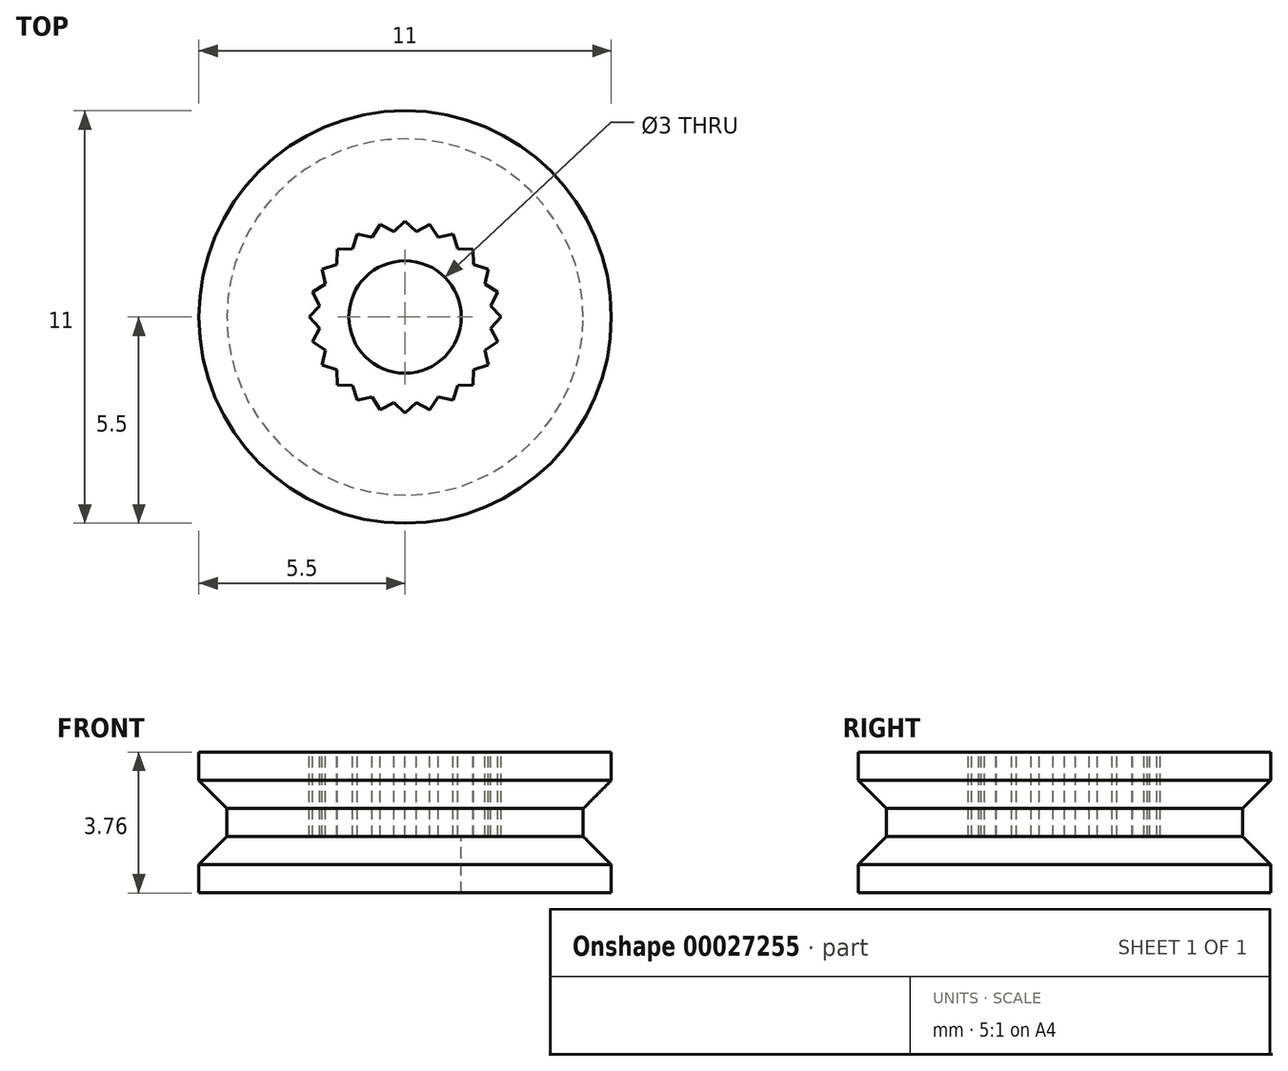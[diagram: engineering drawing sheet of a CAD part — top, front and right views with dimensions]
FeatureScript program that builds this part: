
annotation { "Feature Type Name" : "Feature", "Feature Type Description" : "" }
export const myFeature = defineFeature(function(context is Context, id is Id, definition is map)
    precondition{}
    {
        {
            var Q0;
            Q0=qCreatedBy(makeId("Front.planeOp"),FACE);
            var sketch = newSketch(context, id + "F0", { "sketchPlane" : qUnion([Q0])});
            skLineSegment(sketch, "E0", {"start": v(-1.88, 0) * mm, "end": v(-1.88, 6.25) * mm});
            skLineSegment(sketch, "E1", {"start": v(-1.88, 6.25) * mm, "end": v(-0.38, 4.75) * mm});
            skLineSegment(sketch, "E2", {"start": v(-0.38, 4.75) * mm, "end": v(0.37, 4.75) * mm});
            skLineSegment(sketch, "E3", {"start": v(0.37, 4.75) * mm, "end": v(1.88, 6.25) * mm});
            skLineSegment(sketch, "E4", {"start": v(1.87, 6.25) * mm, "end": v(1.87, 0) * mm});
            skLineSegment(sketch, "E5", {"start": v(1.87, 0) * mm, "end": v(-1.87, 0) * mm});
            skPoint(sketch, "E6", {"position": v(0, 0) * mm});
            skLineSegment(sketch, "E7", {"start": v(-1.88, 5.5) * mm, "end": v(1.87, 5.5) * mm});
            skSolve(sketch);
        }
        {
            var Q0;
            {var subQ10=sQuery(id+"F0.wireOp",EDGE,"E2");Q0=makeQuery(id+"F0.imprint","IMPRINT",FACE,{"disambiguationData":[TD([[makeQuery(id+"F0.imprint","IMPRINT",EDGE,{"derivedFrom":subQ10}),-1.0]])]});}
            var Q1;
            Q1=sQuery(id+"F0.wireOp",EDGE,"E5");
            revolve(context, id + "F1", {"entities" : qUnion([Q0]), "axis" : qUnion([Q1]), "revolveType" : RevolveType.FULL});
        }
        {
            var Q0;
            Q0=makeQuery(id+"F1.opRevolve","SWEPT_FACE",FACE,{"disambiguationData":[OSD([sQuery(id+"F0.wireOp",EDGE,"E4")])]});
            var sketch = newSketch(context, id + "F2", { "sketchPlane" : qUnion([Q0])});
            skCircle(sketch, "E8", {"center": v(0, 0) * mm, "radius": 2.3 * mm, "construction": true});
            skFitSpline(sketch, "E9.4", {"points": [v(-0.66, 2.47) * mm, v(-0.54, 2.4) * mm, v(-0.42, 2.34) * mm, v(-0.3, 2.28) * mm]});
            skFitSpline(sketch, "E9.18", {"points": [v(2.28, -0.3) * mm, v(2.34, -0.42) * mm, v(2.4, -0.54) * mm, v(2.47, -0.66) * mm]});
            skFitSpline(sketch, "E9.32", {"points": [v(-0.66, -2.47) * mm, v(-0.73, -2.35) * mm, v(-0.8, -2.24) * mm, v(-0.88, -2.12) * mm]});
            skFitSpline(sketch, "E9.33", {"points": [v(-0.88, -2.12) * mm, v(-1.01, -2.15) * mm, v(-1.15, -2.18) * mm, v(-1.28, -2.21) * mm]});
            skFitSpline(sketch, "E9.7", {"points": [v(0.3, 2.28) * mm, v(0.42, 2.34) * mm, v(0.54, 2.4) * mm, v(0.66, 2.47) * mm]});
            skCircle(sketch, "E10", {"center": v(0, 0) * mm, "radius": 2.56 * mm, "construction": true});
            skFitSpline(sketch, "E9.34", {"points": [v(-1.28, -2.21) * mm, v(-1.32, -2.08) * mm, v(-1.36, -1.95) * mm, v(-1.4, -1.82) * mm]});
            skFitSpline(sketch, "E9.16", {"points": [v(2.47, 0.66) * mm, v(2.4, 0.54) * mm, v(2.34, 0.42) * mm, v(2.28, 0.3) * mm]});
            skFitSpline(sketch, "E9.13", {"points": [v(1.82, 1.4) * mm, v(1.95, 1.36) * mm, v(2.08, 1.32) * mm, v(2.21, 1.28) * mm]});
            skFitSpline(sketch, "E9.25", {"points": [v(1.4, -1.82) * mm, v(1.36, -1.95) * mm, v(1.32, -2.08) * mm, v(1.28, -2.21) * mm]});
            skFitSpline(sketch, "E9.38", {"points": [v(-2.21, -1.28) * mm, v(-2.18, -1.15) * mm, v(-2.15, -1.01) * mm, v(-2.12, -0.88) * mm]});
            skFitSpline(sketch, "E9.14", {"points": [v(2.21, 1.28) * mm, v(2.18, 1.15) * mm, v(2.15, 1.01) * mm, v(2.12, 0.88) * mm]});
            skFitSpline(sketch, "E9.12", {"points": [v(1.8, 1.8) * mm, v(1.81, 1.67) * mm, v(1.82, 1.54) * mm, v(1.82, 1.4) * mm]});
            skFitSpline(sketch, "E9.31", {"points": [v(-0.3, -2.28) * mm, v(-0.42, -2.34) * mm, v(-0.54, -2.4) * mm, v(-0.66, -2.47) * mm]});
            skFitSpline(sketch, "E9.8", {"points": [v(0.66, 2.47) * mm, v(0.73, 2.35) * mm, v(0.8, 2.24) * mm, v(0.88, 2.12) * mm]});
            skFitSpline(sketch, "E9.39", {"points": [v(-2.12, -0.88) * mm, v(-2.24, -0.8) * mm, v(-2.35, -0.73) * mm, v(-2.47, -0.66) * mm]});
            skFitSpline(sketch, "E9.23", {"points": [v(1.82, -1.4) * mm, v(1.82, -1.54) * mm, v(1.81, -1.67) * mm, v(1.8, -1.8) * mm]});
            skFitSpline(sketch, "E9.47", {"points": [v(-2.12, 0.88) * mm, v(-2.15, 1.01) * mm, v(-2.18, 1.15) * mm, v(-2.21, 1.28) * mm]});
            skFitSpline(sketch, "E9.9", {"points": [v(0.88, 2.12) * mm, v(1.01, 2.15) * mm, v(1.15, 2.18) * mm, v(1.28, 2.21) * mm]});
            skFitSpline(sketch, "E9.36", {"points": [v(-1.8, -1.8) * mm, v(-1.81, -1.67) * mm, v(-1.82, -1.54) * mm, v(-1.82, -1.4) * mm]});
            skFitSpline(sketch, "E9.20", {"points": [v(2.47, -0.66) * mm, v(2.35, -0.73) * mm, v(2.24, -0.8) * mm, v(2.12, -0.88) * mm]});
            skFitSpline(sketch, "E9.15", {"points": [v(2.12, 0.88) * mm, v(2.24, 0.8) * mm, v(2.35, 0.73) * mm, v(2.47, 0.66) * mm]});
            skFitSpline(sketch, "E9.2", {"points": [v(-1.28, 2.21) * mm, v(-1.15, 2.18) * mm, v(-1.01, 2.15) * mm, v(-0.88, 2.12) * mm]});
            skFitSpline(sketch, "E9.26", {"points": [v(1.28, -2.21) * mm, v(1.15, -2.18) * mm, v(1.01, -2.15) * mm, v(0.88, -2.12) * mm]});
            skFitSpline(sketch, "E9.30", {"points": [v(0, -2.56) * mm, v(-0.1, -2.46) * mm, v(-0.2, -2.37) * mm, v(-0.3, -2.28) * mm]});
            skFitSpline(sketch, "E9.43", {"points": [v(-2.28, 0.3) * mm, v(-2.34, 0.42) * mm, v(-2.4, 0.54) * mm, v(-2.47, 0.66) * mm]});
            skFitSpline(sketch, "E9.10", {"points": [v(1.28, 2.21) * mm, v(1.32, 2.08) * mm, v(1.36, 1.95) * mm, v(1.4, 1.82) * mm]});
            skFitSpline(sketch, "E9.11", {"points": [v(1.4, 1.82) * mm, v(1.54, 1.82) * mm, v(1.67, 1.81) * mm, v(1.8, 1.8) * mm]});
            skFitSpline(sketch, "E9.35", {"points": [v(-1.4, -1.82) * mm, v(-1.54, -1.82) * mm, v(-1.67, -1.81) * mm, v(-1.8, -1.8) * mm]});
            skFitSpline(sketch, "E9.21", {"points": [v(2.12, -0.88) * mm, v(2.15, -1.01) * mm, v(2.18, -1.15) * mm, v(2.21, -1.28) * mm]});
            skFitSpline(sketch, "E9.37", {"points": [v(-1.82, -1.4) * mm, v(-1.95, -1.36) * mm, v(-2.08, -1.32) * mm, v(-2.21, -1.28) * mm]});
            skFitSpline(sketch, "E9.40", {"points": [v(-2.47, -0.66) * mm, v(-2.4, -0.54) * mm, v(-2.34, -0.42) * mm, v(-2.28, -0.3) * mm]});
            skFitSpline(sketch, "E9.24", {"points": [v(1.8, -1.8) * mm, v(1.67, -1.81) * mm, v(1.54, -1.82) * mm, v(1.4, -1.82) * mm]});
            skFitSpline(sketch, "E9.29", {"points": [v(0.3, -2.28) * mm, v(0.2, -2.37) * mm, v(0.1, -2.46) * mm, v(0, -2.56) * mm]});
            skFitSpline(sketch, "E9.45", {"points": [v(-1.82, 1.4) * mm, v(-1.82, 1.54) * mm, v(-1.81, 1.67) * mm, v(-1.8, 1.8) * mm]});
            skFitSpline(sketch, "E9.41", {"points": [v(-2.28, -0.3) * mm, v(-2.37, -0.2) * mm, v(-2.46, -0.1) * mm, v(-2.56, 0) * mm]});
            skFitSpline(sketch, "E9.44", {"points": [v(-2.47, 0.66) * mm, v(-2.35, 0.73) * mm, v(-2.24, 0.8) * mm, v(-2.12, 0.88) * mm]});
            skFitSpline(sketch, "E9.28", {"points": [v(0.66, -2.47) * mm, v(0.54, -2.4) * mm, v(0.42, -2.34) * mm, v(0.3, -2.28) * mm]});
            skFitSpline(sketch, "E9.0", {"points": [v(-1.8, 1.8) * mm, v(-1.67, 1.81) * mm, v(-1.54, 1.82) * mm, v(-1.4, 1.82) * mm]});
            skFitSpline(sketch, "E9.5", {"points": [v(-0.3, 2.28) * mm, v(-0.2, 2.37) * mm, v(-0.1, 2.46) * mm, v(0, 2.56) * mm]});
            skFitSpline(sketch, "E9.27", {"points": [v(0.88, -2.12) * mm, v(0.8, -2.24) * mm, v(0.73, -2.35) * mm, v(0.66, -2.47) * mm]});
            skFitSpline(sketch, "E9.1", {"points": [v(-1.4, 1.82) * mm, v(-1.36, 1.95) * mm, v(-1.32, 2.08) * mm, v(-1.28, 2.21) * mm]});
            skFitSpline(sketch, "E9.6", {"points": [v(0, 2.56) * mm, v(0.1, 2.46) * mm, v(0.2, 2.37) * mm, v(0.3, 2.28) * mm]});
            skFitSpline(sketch, "E9.22", {"points": [v(2.21, -1.28) * mm, v(2.08, -1.32) * mm, v(1.95, -1.36) * mm, v(1.82, -1.4) * mm]});
            skFitSpline(sketch, "E9.42", {"points": [v(-2.56, 0) * mm, v(-2.46, 0.1) * mm, v(-2.37, 0.2) * mm, v(-2.28, 0.3) * mm]});
            skFitSpline(sketch, "E9.3", {"points": [v(-0.88, 2.12) * mm, v(-0.8, 2.24) * mm, v(-0.73, 2.35) * mm, v(-0.66, 2.47) * mm]});
            skFitSpline(sketch, "E9.17", {"points": [v(2.28, 0.3) * mm, v(2.37, 0.2) * mm, v(2.46, 0.1) * mm, v(2.56, 0) * mm]});
            skFitSpline(sketch, "E9.46", {"points": [v(-2.21, 1.28) * mm, v(-2.08, 1.32) * mm, v(-1.95, 1.36) * mm, v(-1.82, 1.4) * mm]});
            skFitSpline(sketch, "E9.19", {"points": [v(2.56, 0) * mm, v(2.46, -0.1) * mm, v(2.37, -0.2) * mm, v(2.28, -0.3) * mm]});
            skLineSegment(sketch, "E11", {"start": v(-1.82, 1.4) * mm, "end": v(1.82, -1.4) * mm, "construction": true});
            skCircle(sketch, "E12", {"center": v(0, 0) * mm, "radius": 1.5 * mm});
            skSolve(sketch);
        }
        {
            var Q0;
            Q0=makeQuery(id+"F2.imprint","IMPRINT",FACE,{"disambiguationData":[TD([[makeQuery(id+"F2.imprint","IMPRINT",EDGE,{"derivedFrom":sQuery(id+"F2.wireOp",EDGE,"E9.32")}),-1.0]])]});
            var Q1;
            Q1=makeQuery(id+"F2.imprint","IMPRINT",FACE,{"disambiguationData":[TD([[makeQuery(id+"F2.imprint","IMPRINT",EDGE,{"derivedFrom":sQuery(id+"F2.wireOp",EDGE,"E9.4")}),-1.0]])]});
            extrude(context, id + "F3", {"entities" : qUnion([Q0, Q1]), "operationType" : NewBodyOperationType.REMOVE, "oppositeDirection" : true, "depth" : 2.25 * mm});
        }
        {
            var Q0;
            Q0=makeQuery(id+"F2.imprint","IMPRINT",FACE,{"disambiguationData":[TD([[makeQuery(id+"F2.imprint","IMPRINT",EDGE,{"derivedFrom":sQuery(id+"F2.wireOp",EDGE,"E12")}),1.0]])]});
            var Q1;
            Q1=sQuery(id+"F2.wireOp",EDGE,"E12");
            extrude(context, id + "F4", {"entities" : qUnion([Q0]), "operationType" : NewBodyOperationType.REMOVE, "surfaceEntities" : qUnion([Q1]), "endBound" : BoundingType.THROUGH_ALL, "oppositeDirection" : true, "depth" : 25 * mm});
        }
        {
            var Q0;
            Q0=qCreatedBy(makeId("Top.planeOp"),FACE);
            var sketch = newSketch(context, id + "F5", { "sketchPlane" : qUnion([Q0])});
            skLineSegment(sketch, "E13", {"start": v(-14, 0) * mm, "end": v(17.64, 0) * mm});
            skLineSegment(sketch, "E14", {"start": v(0, -21.28) * mm, "end": v(0, 27.28) * mm});
            skSolve(sketch);
        }
        {
            var Q0;
            Q0=makeQuery(id+"F1.opRevolve","SWEPT_BODY",BODY,{"disambiguationData":[OSD([sQuery(id+"F0.wireOp",EDGE,"E0"),sQuery(id+"F0.wireOp",EDGE,"E1"),sQuery(id+"F0.wireOp",EDGE,"E2"),sQuery(id+"F0.wireOp",EDGE,"E3"),sQuery(id+"F0.wireOp",EDGE,"E4"),sQuery(id+"F0.wireOp",EDGE,"E5"),sQuery(id+"F0.wireOp",EDGE,"E7")])]});
            var Q1;
            Q1=sQuery(id+"F5.wireOp",EDGE,"E14");
            transform(context, id + "F6", {"entities" : qUnion([Q0]), "transformType" : TransformType.ROTATION, "transformAxis" : qUnion([Q1]), "angle" : 270 * degree, "makeCopy" : false});
        }
    });
